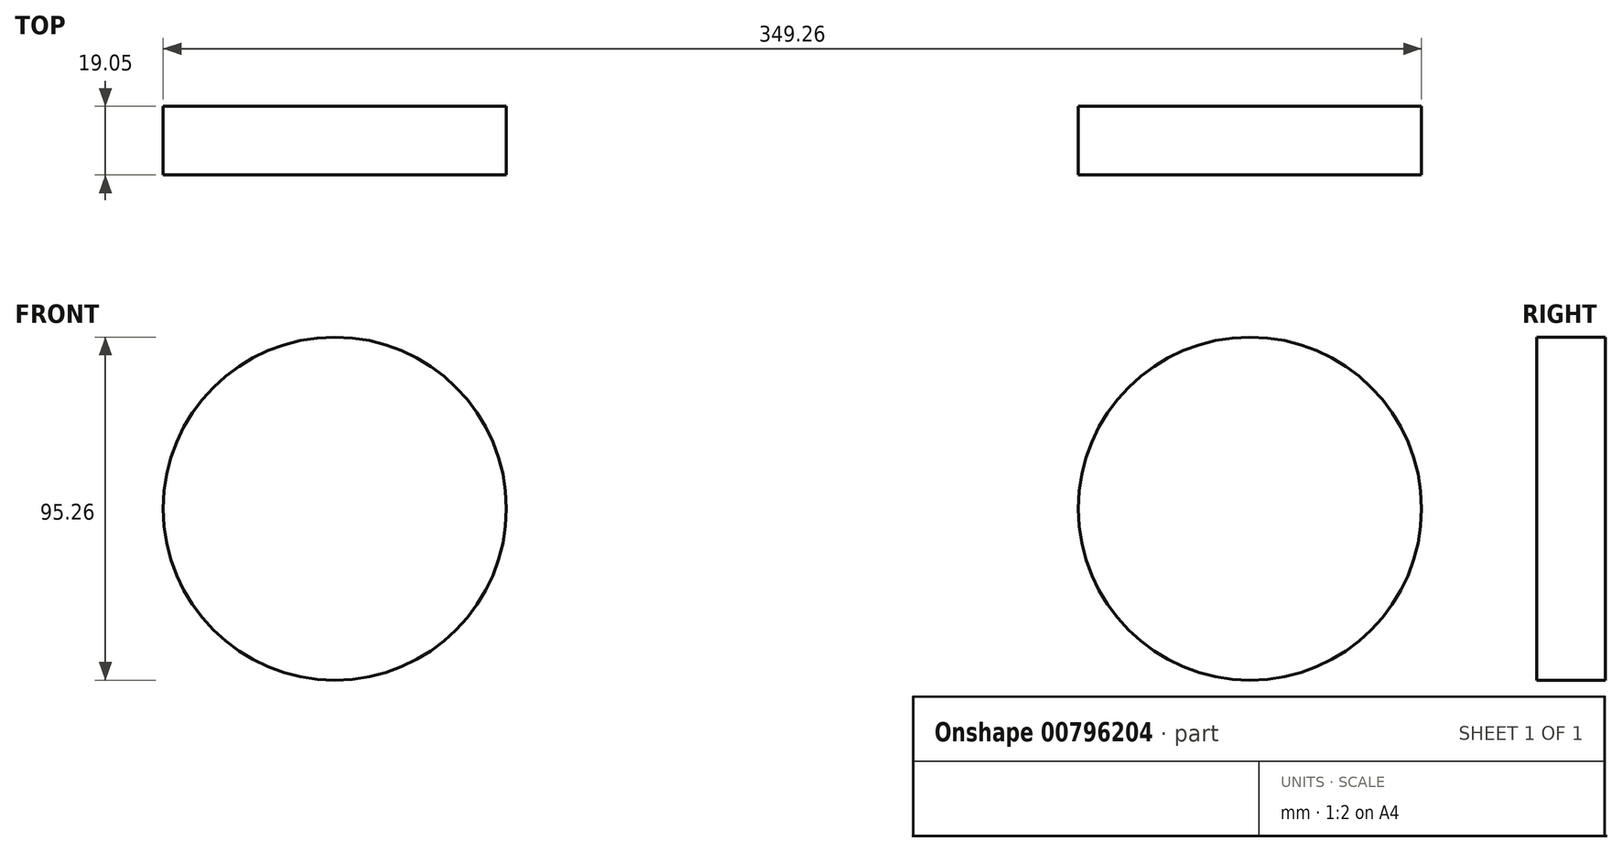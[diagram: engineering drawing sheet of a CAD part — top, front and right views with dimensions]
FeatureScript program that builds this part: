
annotation { "Feature Type Name" : "Feature", "Feature Type Description" : "" }
export const myFeature = defineFeature(function(context is Context, id is Id, definition is map)
    precondition{}
    {
        {
            var Q0;
            Q0=qCreatedBy(makeId("Front.planeOp"),FACE);
            var sketch = newSketch(context, id + "F0", { "sketchPlane" : qUnion([Q0])});
            skLineSegment(sketch, "E0.bottom", {"start": v(0, 0) * mm, "end": v(1016, 0) * mm});
            skLineSegment(sketch, "E0.top", {"start": v(0, -146.05) * mm, "end": v(1016, -146.05) * mm});
            skLineSegment(sketch, "E0.left", {"start": v(0, 0) * mm, "end": v(0, -146.05) * mm});
            skLineSegment(sketch, "E0.right", {"start": v(1016, 0) * mm, "end": v(1016, -146.05) * mm});
            skSolve(sketch);
        }
        {
            var Q0;
            Q0=makeQuery(id+"F0.imprint","IMPRINT",FACE,{"disambiguationData":[TD([[makeQuery(id+"F0.imprint","IMPRINT",EDGE,{"derivedFrom":sQuery(id+"F0.wireOp",EDGE,"E0.bottom")}),-1.0]])]});
            extrude(context, id + "F1", {"entities" : qUnion([Q0]), "depth" : 19.05 * mm, "offsetDistance" : 25.4 * mm});
        }
        {
            var Q0;
            Q0=makeQuery(id+"F1.opExtrude","CAP_FACE",FACE,{"disambiguationData":[OSD([sQuery(id+"F0.wireOp",EDGE,"E0.bottom"),sQuery(id+"F0.wireOp",EDGE,"E0.top"),sQuery(id+"F0.wireOp",EDGE,"E0.left"),sQuery(id+"F0.wireOp",EDGE,"E0.right")])],"isStart":false});
            var sketch = newSketch(context, id + "F2", { "sketchPlane" : qUnion([Q0])});
            skLineSegment(sketch, "E1", {"start": v(254, -63.5) * mm, "end": v(508, -63.5) * mm, "construction": true});
            skLineSegment(sketch, "E2", {"start": v(254, -63.5) * mm, "end": v(0, -63.5) * mm, "construction": true});
            skCircle(sketch, "E3", {"center": v(381, -63.5) * mm, "radius": 47.63 * mm});
            skCircle(sketch, "E4", {"center": v(127, -63.5) * mm, "radius": 47.63 * mm});
            skLineSegment(sketch, "E5", {"start": v(508, -63.5) * mm, "end": v(508, 0) * mm, "construction": true});
            skCircle(sketch, "E6.MirrorC", {"center": v(635, -63.5) * mm, "radius": 47.63 * mm});
            skCircle(sketch, "E7.MirrorC", {"center": v(889, -63.5) * mm, "radius": 47.63 * mm});
            skSolve(sketch);
        }
        {
            var Q0;
            Q0=makeQuery(id+"F2.imprint","IMPRINT",FACE,{"disambiguationData":[TD([[makeQuery(id+"F2.imprint","IMPRINT",EDGE,{"derivedFrom":sQuery(id+"F2.wireOp",EDGE,"E4")}),1.0]])]});
            var Q1;
            Q1=makeQuery(id+"F2.imprint","IMPRINT",FACE,{"disambiguationData":[TD([[makeQuery(id+"F2.imprint","IMPRINT",EDGE,{"derivedFrom":sQuery(id+"F2.wireOp",EDGE,"E3")}),1.0]])]});
            var Q2;
            Q2=makeQuery(id+"F2.imprint","IMPRINT",FACE,{"disambiguationData":[TD([[makeQuery(id+"F2.imprint","IMPRINT",EDGE,{"derivedFrom":sQuery(id+"F2.wireOp",EDGE,"9fc2e8fd-1087-41d7-b216-a3ee0542a21c0.MirrorC")}),-1.0]])]});
            var Q3;
            Q3=makeQuery(id+"F2.imprint","IMPRINT",FACE,{"disambiguationData":[TD([[makeQuery(id+"F2.imprint","IMPRINT",EDGE,{"derivedFrom":sQuery(id+"F2.wireOp",EDGE,"3cf50433-0831-45c8-b75f-ac576810fd310.MirrorC")}),-1.0]])]});
            var Q4;
            Q4=makeQuery(id+"F2.imprint","IMPRINT",FACE,{"disambiguationData":[TD([[makeQuery(id+"F2.imprint","IMPRINT",EDGE,{"derivedFrom":sQuery(id+"F2.wireOp",EDGE,"E6.MirrorC")}),-1.0]])]});
            var Q5;
            Q5=makeQuery(id+"F2.imprint","IMPRINT",FACE,{"disambiguationData":[TD([[makeQuery(id+"F2.imprint","IMPRINT",EDGE,{"derivedFrom":sQuery(id+"F2.wireOp",EDGE,"c56d2053-9c2f-483d-aa1d-fea8d3949a620.MirrorC")}),-1.0]])]});
            var Q6;
            Q6=makeQuery(id+"F2.imprint","IMPRINT",FACE,{"disambiguationData":[TD([[makeQuery(id+"F2.imprint","IMPRINT",EDGE,{"derivedFrom":sQuery(id+"F2.wireOp",EDGE,"E7.MirrorC")}),-1.0]])]});
            extrude(context, id + "F3", {"entities" : qUnion([Q0, Q1, Q2, Q3, Q4, Q5, Q6]), "operationType" : NewBodyOperationType.REMOVE, "endBound" : BoundingType.THROUGH_ALL, "oppositeDirection" : true, "depth" : 25.4 * mm, "offsetDistance" : 25.4 * mm});
        }
    });
